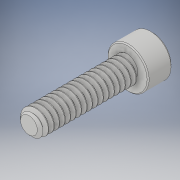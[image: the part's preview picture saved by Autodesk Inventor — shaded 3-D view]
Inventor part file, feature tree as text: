
AUTODESK INVENTOR PART (.ipt)
format: ipt  version: 2018 (Build 220112000, 112)  size: 748,032 bytes
history: native  units: in
note: dims shown in document units (in); Inventor stores cm internally (conversion verified against a paired STEP export)
features: chamfer x1
ambient origin geometry x8: Origin, YZ Plane, XZ Plane, XY Plane, X Axis, Y Axis, Z Axis, Center Point
bodies: Solid1 (feature_tree)
feature tree (1):
  chamfer  "Chamfer2"  [1 undecoded]
note: 1 required parameter value undecoded (feature->parameter linkage not recoverable at this tier; creation-order binding heuristic only, values carry confidence <= 0.55)
